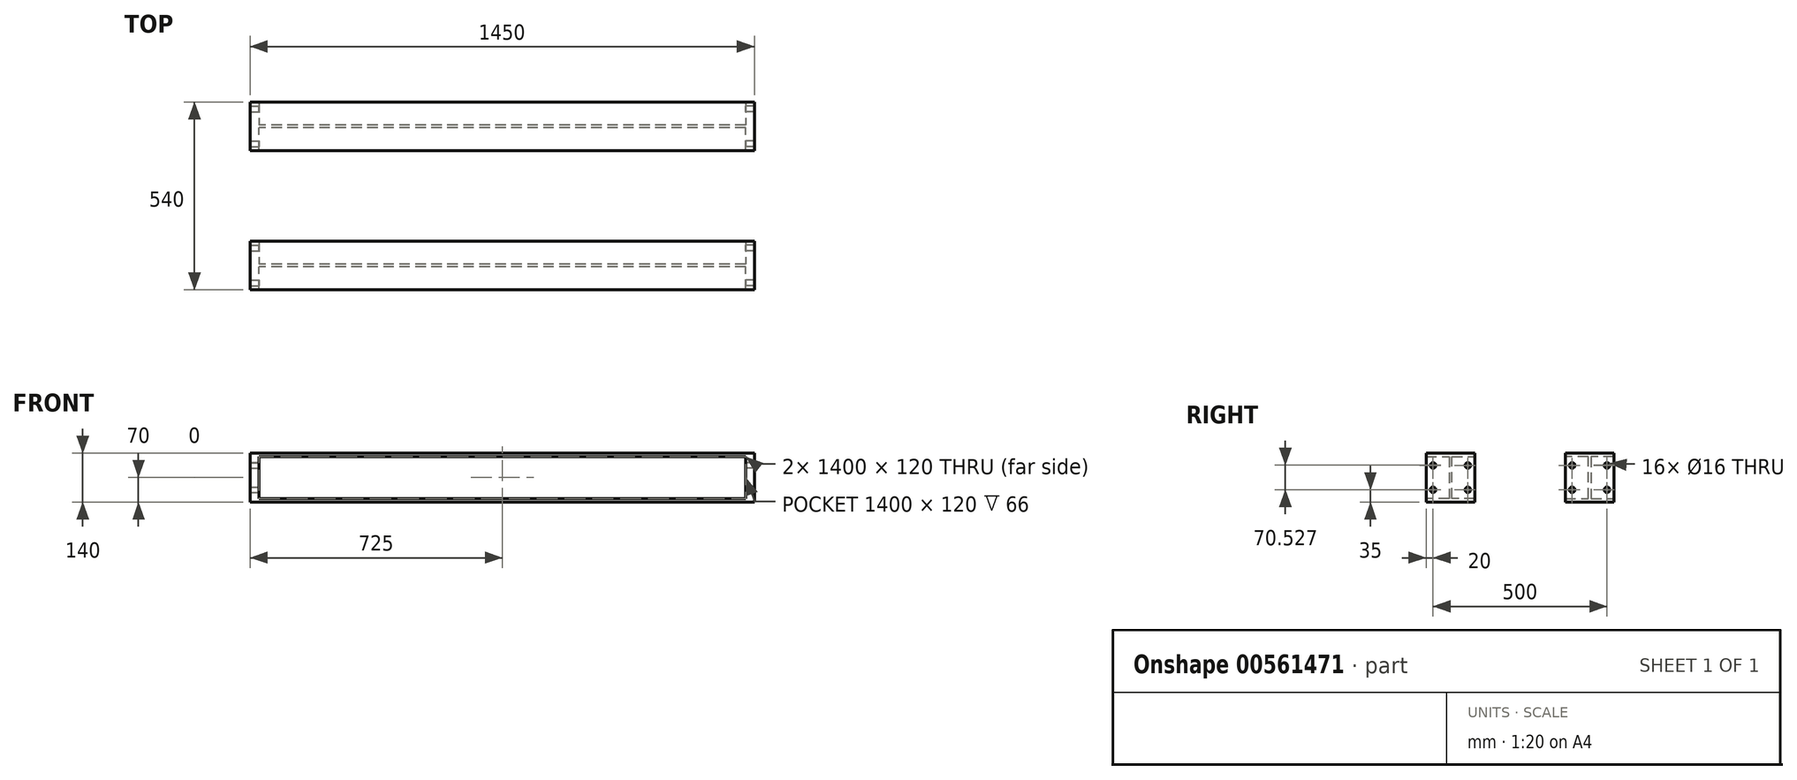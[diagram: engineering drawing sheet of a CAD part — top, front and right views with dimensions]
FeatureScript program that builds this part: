
annotation { "Feature Type Name" : "Feature", "Feature Type Description" : "" }
export const myFeature = defineFeature(function(context is Context, id is Id, definition is map)
    precondition{}
    {
        {
            var Q0;
            Q0=qCreatedBy(makeId("Right.planeOp"),FACE);
            var sketch = newSketch(context, id + "F0", { "sketchPlane" : qUnion([Q0])});
            skLineSegment(sketch, "E0", {"start": v(-270, 60) * mm, "end": v(-204, 60) * mm});
            skLineSegment(sketch, "E1", {"start": v(-204, 60) * mm, "end": v(-204, 0) * mm});
            skLineSegment(sketch, "E2", {"start": v(-204, 0) * mm, "end": v(-204, -60) * mm});
            skLineSegment(sketch, "E3", {"start": v(-204, -60) * mm, "end": v(-270, -60) * mm});
            skLineSegment(sketch, "E4", {"start": v(-270, -60) * mm, "end": v(-270, -70) * mm});
            skLineSegment(sketch, "E5", {"start": v(-270, -70) * mm, "end": v(-130, -70) * mm});
            skLineSegment(sketch, "E6", {"start": v(-130, -70) * mm, "end": v(-130, -60) * mm});
            skLineSegment(sketch, "E7", {"start": v(-130, -60) * mm, "end": v(-196, -60) * mm});
            skLineSegment(sketch, "E8", {"start": v(-196, -60) * mm, "end": v(-196, 60) * mm});
            skLineSegment(sketch, "E9", {"start": v(-196, 60) * mm, "end": v(-130, 60) * mm});
            skLineSegment(sketch, "E10", {"start": v(-130, 60) * mm, "end": v(-130, 70) * mm});
            skLineSegment(sketch, "E11", {"start": v(-130, 70) * mm, "end": v(-270, 70) * mm});
            skLineSegment(sketch, "E12", {"start": v(-270, 70) * mm, "end": v(-270, 60) * mm});
            skSolve(sketch);
        }
        {
            var Q0;
            Q0=makeQuery(id+"F0.imprint","IMPRINT",FACE,{"disambiguationData":[TD([[makeQuery(id+"F0.imprint","IMPRINT",EDGE,{"derivedFrom":sQuery(id+"F0.wireOp",EDGE,"E0")}),1.0]])]});
            extrude(context, id + "F1", {"entities" : qUnion([Q0]), "endBound" : BoundingType.SYMMETRIC, "depth" : 1400 * mm, "offsetDistance" : 25 * mm});
        }
        {
            var Q0;
            Q0=makeQuery(id+"F1.opExtrude","CAP_FACE",FACE,{"disambiguationData":[OSD([sQuery(id+"F0.wireOp",EDGE,"E0"),sQuery(id+"F0.wireOp",EDGE,"E1"),sQuery(id+"F0.wireOp",EDGE,"E2"),sQuery(id+"F0.wireOp",EDGE,"E3"),sQuery(id+"F0.wireOp",EDGE,"E4"),sQuery(id+"F0.wireOp",EDGE,"E5"),sQuery(id+"F0.wireOp",EDGE,"E6"),sQuery(id+"F0.wireOp",EDGE,"E7"),sQuery(id+"F0.wireOp",EDGE,"E8"),sQuery(id+"F0.wireOp",EDGE,"E9"),sQuery(id+"F0.wireOp",EDGE,"E10"),sQuery(id+"F0.wireOp",EDGE,"E11"),sQuery(id+"F0.wireOp",EDGE,"E12")])],"isStart":false});
            var sketch = newSketch(context, id + "F2", { "sketchPlane" : qUnion([Q0])});
            skLineSegment(sketch, "E13", {"start": v(-270, 70) * mm, "end": v(-130, 70) * mm});
            skLineSegment(sketch, "E14", {"start": v(-130, 70) * mm, "end": v(-130, -70) * mm});
            skLineSegment(sketch, "E15", {"start": v(-130, -70) * mm, "end": v(-270, -70) * mm});
            skLineSegment(sketch, "E16", {"start": v(-270, -70) * mm, "end": v(-270, 70) * mm});
            skCircle(sketch, "E17", {"center": v(-250, 35) * mm, "radius": 8 * mm});
            skCircle(sketch, "E18", {"center": v(-250, -35) * mm, "radius": 8 * mm});
            skCircle(sketch, "E19", {"center": v(-150, 35) * mm, "radius": 8 * mm});
            skCircle(sketch, "E20", {"center": v(-150, -35) * mm, "radius": 8 * mm});
            skSolve(sketch);
        }
        {
            var Q0;
            {var subQ4=sQuery(id+"F2.wireOp",EDGE,"E13");Q0=makeQuery(id+"F2.imprint","IMPRINT",FACE,{"disambiguationData":[TD([[makeQuery(id+"F2.imprint","IMPRINT",EDGE,{"derivedFrom":subQ4}),1.0]])]});}
            var Q1;
            Q1=makeQuery(id+"F2.imprint","IMPRINT",FACE,{"disambiguationData":[TD([[makeQuery(id+"F2.imprint","IMPRINT",EDGE,{"derivedFrom":sQuery(id+"F2.wireOp",EDGE,"E19")}),-1.0]])]});
            var Q2;
            Q2=makeQuery(id+"F2.imprint","IMPRINT",FACE,{"disambiguationData":[TD([[makeQuery(id+"F2.imprint","IMPRINT",EDGE,{"derivedFrom":sQuery(id+"F2.wireOp",EDGE,"E17")}),-1.0]])]});
            extrude(context, id + "F3", {"entities" : qUnion([Q0, Q1, Q2]), "operationType" : NewBodyOperationType.ADD, "depth" : 25 * mm, "offsetDistance" : 25 * mm});
        }
        {
            var Q0;
            Q0=makeQuery(id+"F1.opExtrude","CAP_FACE",FACE,{"disambiguationData":[OSD([sQuery(id+"F0.wireOp",EDGE,"E0"),sQuery(id+"F0.wireOp",EDGE,"E1"),sQuery(id+"F0.wireOp",EDGE,"E2"),sQuery(id+"F0.wireOp",EDGE,"E3"),sQuery(id+"F0.wireOp",EDGE,"E4"),sQuery(id+"F0.wireOp",EDGE,"E5"),sQuery(id+"F0.wireOp",EDGE,"E6"),sQuery(id+"F0.wireOp",EDGE,"E7"),sQuery(id+"F0.wireOp",EDGE,"E8"),sQuery(id+"F0.wireOp",EDGE,"E9"),sQuery(id+"F0.wireOp",EDGE,"E10"),sQuery(id+"F0.wireOp",EDGE,"E11"),sQuery(id+"F0.wireOp",EDGE,"E12")])],"isStart":true});
            var sketch = newSketch(context, id + "F4", { "sketchPlane" : qUnion([Q0])});
            skLineSegment(sketch, "E21.bottom", {"start": v(130, 70) * mm, "end": v(270, 70) * mm});
            skLineSegment(sketch, "E21.top", {"start": v(130, -70) * mm, "end": v(270, -70) * mm});
            skLineSegment(sketch, "E21.left", {"start": v(130, 70) * mm, "end": v(130, -70) * mm});
            skLineSegment(sketch, "E21.right", {"start": v(270, 70) * mm, "end": v(270, -70) * mm});
            skCircle(sketch, "E22", {"center": v(150, 35) * mm, "radius": 8 * mm});
            skCircle(sketch, "E23", {"center": v(150, -35) * mm, "radius": 8 * mm});
            skCircle(sketch, "E24", {"center": v(250, 35.53) * mm, "radius": 8 * mm});
            skCircle(sketch, "E25", {"center": v(250, -35) * mm, "radius": 8 * mm});
            skSolve(sketch);
        }
        {
            var Q0;
            {var subQ4=sQuery(id+"F4.wireOp",EDGE,"E21.bottom");Q0=makeQuery(id+"F4.imprint","IMPRINT",FACE,{"disambiguationData":[TD([[makeQuery(id+"F4.imprint","IMPRINT",EDGE,{"derivedFrom":subQ4}),-1.0]])]});}
            var Q1;
            Q1=makeQuery(id+"F4.imprint","IMPRINT",FACE,{"disambiguationData":[TD([[makeQuery(id+"F4.imprint","IMPRINT",EDGE,{"derivedFrom":sQuery(id+"F4.wireOp",EDGE,"E22")}),-1.0]])]});
            var Q2;
            Q2=makeQuery(id+"F4.imprint","IMPRINT",FACE,{"disambiguationData":[TD([[makeQuery(id+"F4.imprint","IMPRINT",EDGE,{"derivedFrom":sQuery(id+"F4.wireOp",EDGE,"E24")}),-1.0]])]});
            extrude(context, id + "F5", {"entities" : qUnion([Q0, Q1, Q2]), "operationType" : NewBodyOperationType.ADD, "depth" : 25 * mm, "offsetDistance" : 25 * mm});
        }
        {
            var Q0;
            Q0=makeQuery(id+"F1.opExtrude","SWEPT_BODY",BODY,{"disambiguationData":[OSD([sQuery(id+"F0.wireOp",EDGE,"E0"),sQuery(id+"F0.wireOp",EDGE,"E1"),sQuery(id+"F0.wireOp",EDGE,"E2"),sQuery(id+"F0.wireOp",EDGE,"E3"),sQuery(id+"F0.wireOp",EDGE,"E4"),sQuery(id+"F0.wireOp",EDGE,"E5"),sQuery(id+"F0.wireOp",EDGE,"E6"),sQuery(id+"F0.wireOp",EDGE,"E7"),sQuery(id+"F0.wireOp",EDGE,"E8"),sQuery(id+"F0.wireOp",EDGE,"E9"),sQuery(id+"F0.wireOp",EDGE,"E10"),sQuery(id+"F0.wireOp",EDGE,"E11"),sQuery(id+"F0.wireOp",EDGE,"E12")])]});
            var Q1;
            Q1=qCreatedBy(makeId("Front.planeOp"),FACE);
            mirror(context, id + "F6", {"entities" : qUnion([Q0]), "mirrorPlane" : qUnion([Q1])});
        }
    });
